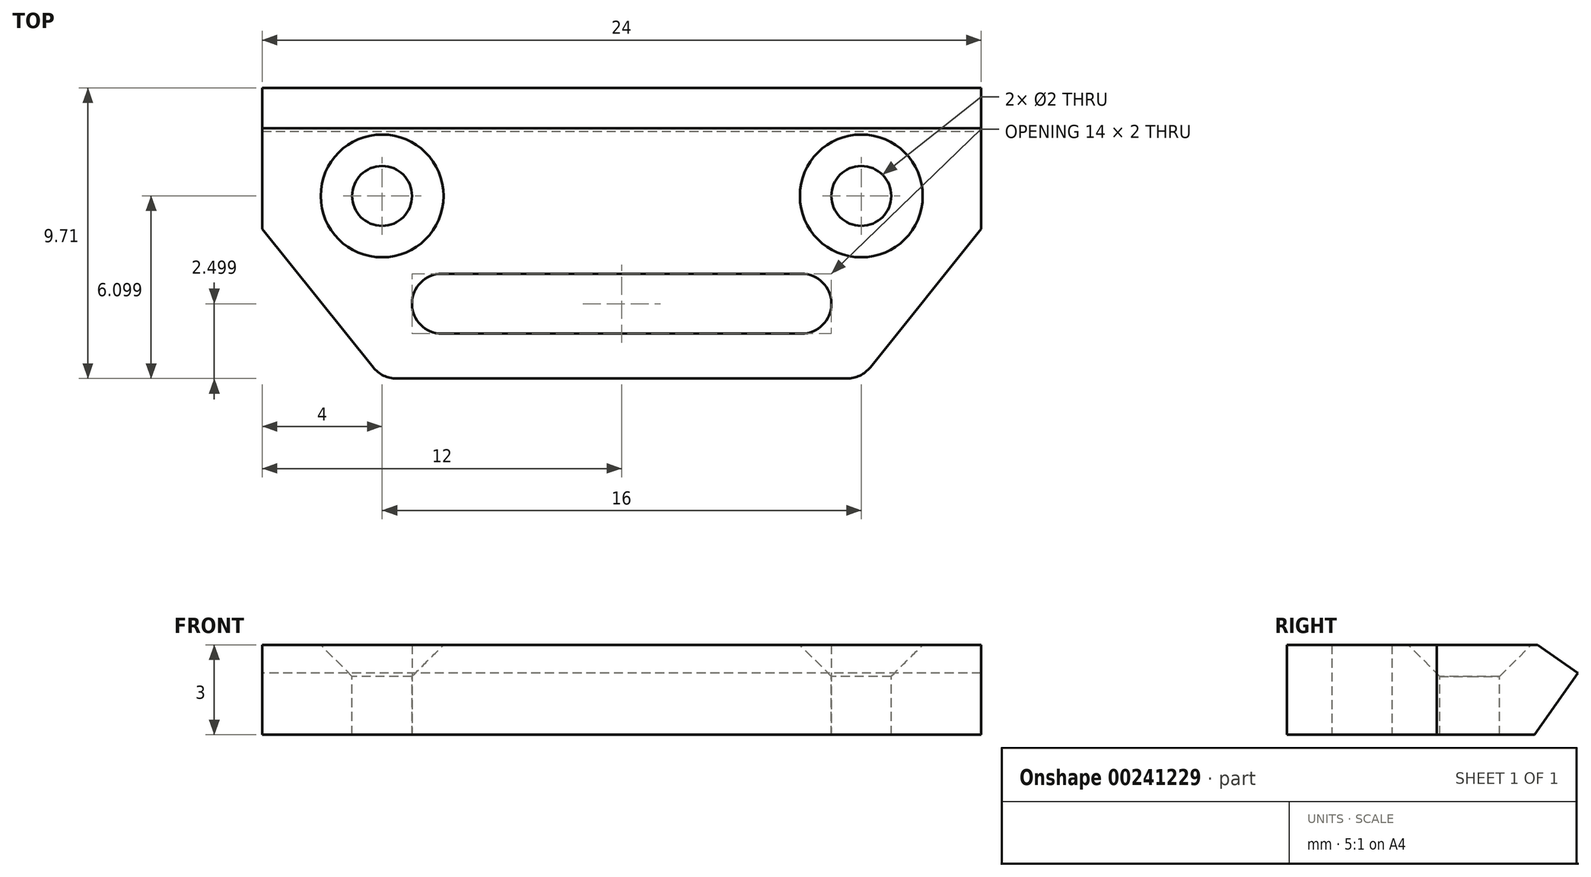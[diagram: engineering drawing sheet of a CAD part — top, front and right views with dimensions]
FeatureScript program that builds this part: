
annotation { "Feature Type Name" : "Feature", "Feature Type Description" : "" }
export const myFeature = defineFeature(function(context is Context, id is Id, definition is map)
    precondition{}
    {
        {
            var Q0;
            Q0=qCreatedBy(makeId("Top.planeOp"),FACE);
            var sketch = newSketch(context, id + "F0", { "sketchPlane" : qUnion([Q0])});
            skLineSegment(sketch, "E0", {"start": v(12, 5.47) * mm, "end": v(8, 0.47) * mm});
            skLineSegment(sketch, "E1", {"start": v(-8, 0.47) * mm, "end": v(-12, 5.47) * mm});
            skLineSegment(sketch, "E2.bottom", {"start": v(-7, 3.97) * mm, "end": v(7, 3.97) * mm});
            skLineSegment(sketch, "E2.top", {"start": v(-7, 1.97) * mm, "end": v(7, 1.97) * mm});
            skLineSegment(sketch, "E2.left", {"start": v(-7, 3.97) * mm, "end": v(-7, 1.97) * mm});
            skLineSegment(sketch, "E2.right", {"start": v(7, 3.97) * mm, "end": v(7, 1.97) * mm});
            skLineSegment(sketch, "E3", {"start": v(-12, 5.47) * mm, "end": v(-12, 10.47) * mm});
            skLineSegment(sketch, "E4", {"start": v(-12, 10.47) * mm, "end": v(12, 10.47) * mm});
            skLineSegment(sketch, "E5", {"start": v(12, 10.47) * mm, "end": v(12, 5.47) * mm});
            skLineSegment(sketch, "E6", {"start": v(-8, 0.47) * mm, "end": v(8, 0.47) * mm});
            skSolve(sketch);
        }
        {
            var Q0;
            Q0 = qSketchRegion(id + "F0", true);
            extrude(context, id + "F1", {"entities" : qUnion([Q0]), "depth" : 3 * mm});
        }
        {
            var Q0;
            Q0=makeQuery(id+"F1.opExtrude","SWEPT_EDGE",EDGE,{"disambiguationData":[OSD([sQuery(id+"F0.wireOp",EDGE,"E2.bottom"),sQuery(id+"F0.wireOp",EDGE,"E2.left")])]});
            var Q1;
            Q1=makeQuery(id+"F1.opExtrude","SWEPT_EDGE",EDGE,{"disambiguationData":[OSD([sQuery(id+"F0.wireOp",EDGE,"E2.top"),sQuery(id+"F0.wireOp",EDGE,"E2.left")])]});
            var Q2;
            Q2=makeQuery(id+"F1.opExtrude","SWEPT_EDGE",EDGE,{"disambiguationData":[OSD([sQuery(id+"F0.wireOp",EDGE,"E2.bottom"),sQuery(id+"F0.wireOp",EDGE,"E2.right")])]});
            var Q3;
            Q3=makeQuery(id+"F1.opExtrude","SWEPT_EDGE",EDGE,{"disambiguationData":[OSD([sQuery(id+"F0.wireOp",EDGE,"E2.top"),sQuery(id+"F0.wireOp",EDGE,"E2.right")])]});
            fillet(context, id + "F2", {"entities" : qUnion([Q0, Q1, Q2, Q3]), "radius" : 0.99 * mm, "tangentPropagation" : true, "allowEdgeOverflow" : false});
        }
        {
            var Q0;
            Q0=qCreatedBy(makeId("Right.planeOp"),FACE);
            var sketch = newSketch(context, id + "F3", { "sketchPlane" : qUnion([Q0])});
            skLineSegment(sketch, "E7", {"start": v(10.97, 3.2) * mm, "end": v(8.17, -0.8) * mm});
            skLineSegment(sketch, "E8", {"start": v(8.17, -0.8) * mm, "end": v(10.97, -0.8) * mm});
            skLineSegment(sketch, "E9", {"start": v(10.97, -0.8) * mm, "end": v(10.97, 3.2) * mm});
            skSolve(sketch);
        }
        {
            var Q0;
            Q0 = qSketchRegion(id + "F3", true);
            extrude(context, id + "F4", {"entities" : qUnion([Q0]), "operationType" : NewBodyOperationType.REMOVE, "oppositeDirection" : true, "depth" : 25 * mm, "hasSecondDirection" : true, "secondDirectionOppositeDirection" : false, "secondDirectionDepth" : 25 * mm});
        }
        {
            var Q0;
            Q0=makeQuery(id+"F1.opExtrude","SWEPT_EDGE",EDGE,{"disambiguationData":[OSD([sQuery(id+"F0.wireOp",EDGE,"E0"),sQuery(id+"F0.wireOp",EDGE,"E6")])]});
            var Q1;
            Q1=makeQuery(id+"F1.opExtrude","SWEPT_EDGE",EDGE,{"disambiguationData":[OSD([sQuery(id+"F0.wireOp",EDGE,"E1"),sQuery(id+"F0.wireOp",EDGE,"E6")])]});
            fillet(context, id + "F5", {"entities" : qUnion([Q0, Q1]), "radius" : 1 * mm, "tangentPropagation" : true, "allowEdgeOverflow" : false});
        }
        {
            var Q0;
            Q0=qCreatedBy(makeId("Right.planeOp"),FACE);
            var sketch = newSketch(context, id + "F6", { "sketchPlane" : qUnion([Q0])});
            skLineSegment(sketch, "E10", {"start": v(8.12, 3.5) * mm, "end": v(12.12, 0.7) * mm});
            skLineSegment(sketch, "E11", {"start": v(12.12, 0.7) * mm, "end": v(12.12, 3.5) * mm});
            skLineSegment(sketch, "E12", {"start": v(12.12, 3.5) * mm, "end": v(8.12, 3.5) * mm});
            skSolve(sketch);
        }
        {
            var Q0;
            Q0 = qSketchRegion(id + "F6", true);
            extrude(context, id + "F7", {"entities" : qUnion([Q0]), "operationType" : NewBodyOperationType.REMOVE, "depth" : 25 * mm, "hasSecondDirection" : true, "secondDirectionOppositeDirection" : true, "secondDirectionDepth" : 25 * mm});
        }
        {
            var Q0;
            Q0=qCreatedBy(makeId("Top.planeOp"),FACE);
            cPlane(context, id + "F8", {"entities" : qUnion([Q0]), "cplaneType" : CPlaneType.OFFSET, "offset" : 3 * mm, "width" : 150 * mm, "height" : 150 * mm});
        }
        {
            var Q0;
            Q0=qCreatedBy(id+"F8.planeOp",FACE);
            var sketch = newSketch(context, id + "F9", { "sketchPlane" : qUnion([Q0])});
            skPoint(sketch, "E13", {"position": v(-8, 6.57) * mm});
            skLineSegment(sketch, "E14", {"start": v(0, 15.58) * mm, "end": v(0, -7.95) * mm, "construction": true});
            skPoint(sketch, "E15.MirrorP", {"position": v(8, 6.57) * mm});
            skSolve(sketch);
        }
        {
            var Q0;
            Q0=sQuery(id+"F9.wireOp",VERTEX,"E13");
            var Q1;
            Q1=sQuery(id+"F9.wireOp",VERTEX,"E15.MirrorP");
            var Q2;
            Q2=makeQuery(id+"F1.opExtrude","SWEPT_BODY",BODY,{"disambiguationData":[OSD([sQuery(id+"F0.wireOp",EDGE,"E0"),sQuery(id+"F0.wireOp",EDGE,"E1"),sQuery(id+"F0.wireOp",EDGE,"E2.bottom"),sQuery(id+"F0.wireOp",EDGE,"E2.top"),sQuery(id+"F0.wireOp",EDGE,"E2.left"),sQuery(id+"F0.wireOp",EDGE,"E2.right"),sQuery(id+"F0.wireOp",EDGE,"E3"),sQuery(id+"F0.wireOp",EDGE,"E4"),sQuery(id+"F0.wireOp",EDGE,"E5"),sQuery(id+"F0.wireOp",EDGE,"E6")])]});
            hole(context, id + "F10", {"style" : HoleStyle.C_SINK, "endStyle" : HoleEndStyle.BLIND, "holeDiameter" : 2 * mm, "cSinkDiameter" : 4.1 * mm, "cSinkAngle" : 90 * degree, "holeDepth" : 4 * mm, "tappedDepth" : 12 * mm, "tapClearance" : 3, "locations" : qUnion([Q0, Q1]), "scope" : qUnion([Q2])});
        }
    });
